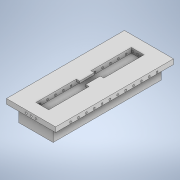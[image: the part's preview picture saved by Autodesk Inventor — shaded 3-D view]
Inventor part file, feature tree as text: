
AUTODESK INVENTOR PART (.ipt)
format: ipt  version: 2021 (Build 250183000, 183)  size: 198,144 bytes
history: native  units: mm
features: sketch x5, extrude x3, plane x2, hole x2, pattern_linear x2, mirror x2
ambient origin geometry x8: Origin, YZ Plane, XZ Plane, XY Plane, X Axis, Y Axis, Z Axis, Center Point
bodies: Solid1 (feature_tree)
feature tree (16):
  plane  "Work Plane1"
  plane  "Work Plane2"
  extrude  "Extrusion1"  Depth=120.0mm
  extrude  "Extrusion2"  Depth=97.0mm
  extrude  "Extrusion3"  Depth=18.5mm
  hole  "Hole1"  [1 undecoded]
  pattern_linear  "Rectangular Pattern1"  Count1=11  [1 undecoded]
  mirror  "Mirror1"
  hole  "Hole2"  [1 undecoded]
  pattern_linear  "Rectangular Pattern2"  Spacing1=5.0mm  [1 undecoded]
  mirror  "Mirror2"
  sketch  "Sketch1"  dims[d0=50.0mm d1=120.0mm]
  sketch  "Sketch2"  dims[d2=13.0mm d3=97.0mm]
  sketch  "Sketch4"  dims[d4=11.5mm d5=18.5mm]
  sketch  "Sketch6"  dims[d6=3.0mm d7=0.0mm d8=35.0mm d9=110.0mm]
  sketch  "Sketch8"  dims[d12=15.0mm d13=0.0mm d14=7.5mm d15=5.0mm d16=15.0mm d17=3.5mm d18=3.5mm d19=41.0mm d20=2.0mm d21=0.0mm d22=2.0mm d23=6.0mm d24=4.0mm d25=2.0mm d26=90.0deg d27=8.0mm d28=20.594885mm d29=120.0mm d31=8.0mm d32=25.0mm d33=60.0mm d34=2.0mm d35=6.0mm d36=4.0mm d37=2.0mm d38=90.0deg d39=8.0mm d40=20.594885mm d41=30.0mm d43=5.0mm]
note: 4 required parameter values undecoded (feature->parameter linkage not recoverable at this tier; creation-order binding heuristic only, values carry confidence <= 0.55)
